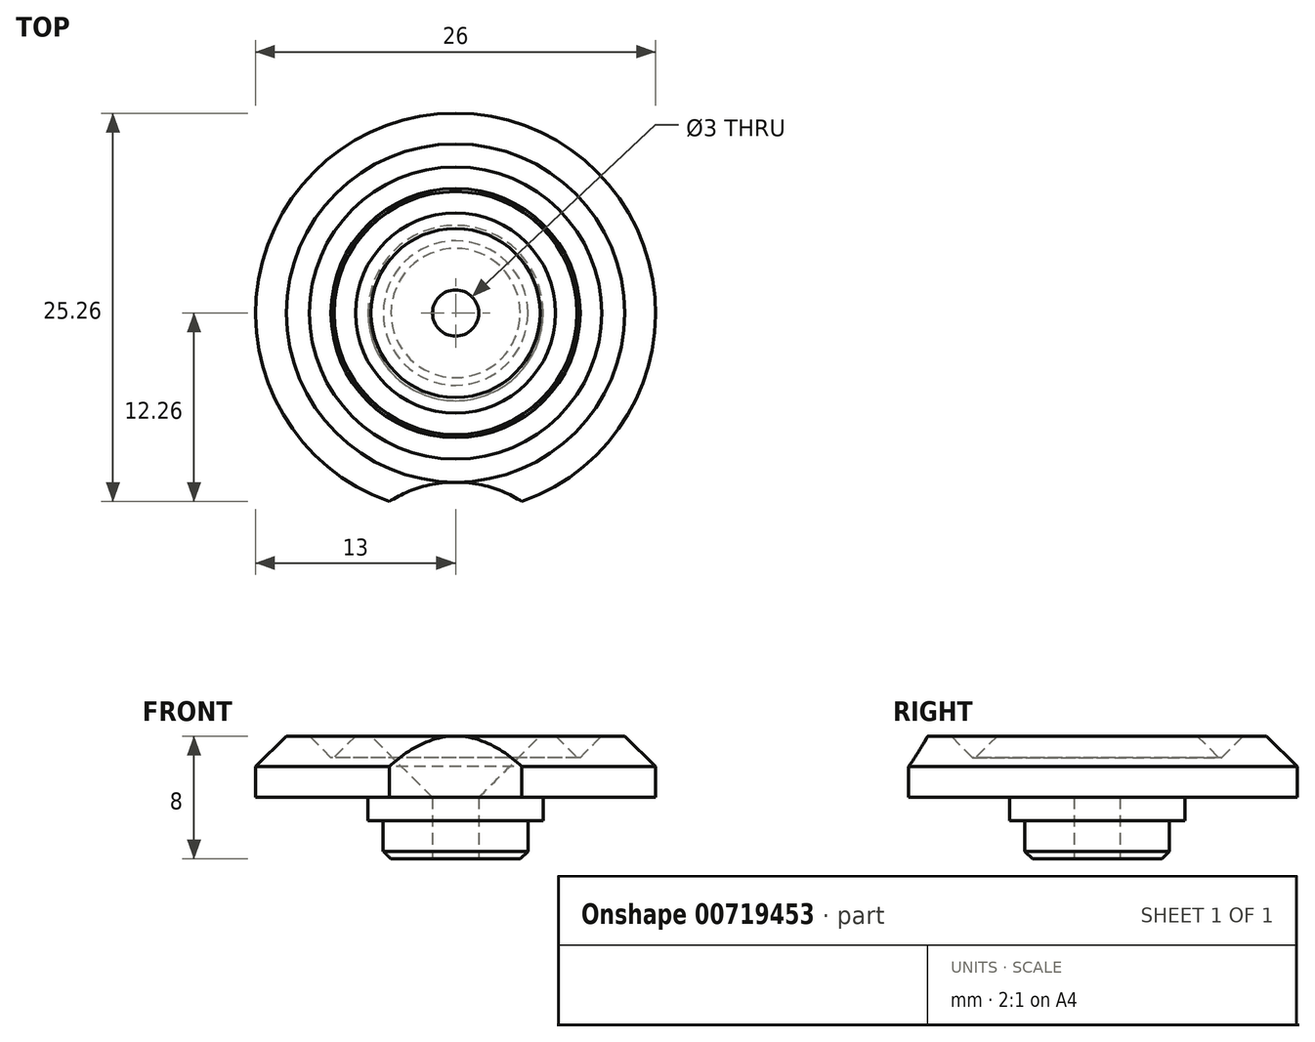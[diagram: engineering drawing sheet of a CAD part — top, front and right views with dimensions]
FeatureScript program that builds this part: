
annotation { "Feature Type Name" : "Feature", "Feature Type Description" : "" }
export const myFeature = defineFeature(function(context is Context, id is Id, definition is map)
    precondition{}
    {
        {
            var Q0;
            Q0=qCreatedBy(makeId("Top.planeOp"),FACE);
            var sketch = newSketch(context, id + "F0", { "sketchPlane" : qUnion([Q0])});
            skCircle(sketch, "E0", {"center": v(0, 0) * mm, "radius": 13 * mm});
            skLineSegment(sketch, "E1", {"start": v(0, 33.5) * mm, "end": v(0, -39.1) * mm, "construction": true});
            skLineSegment(sketch, "E2", {"start": v(30.36, 0) * mm, "end": v(-36.49, 0) * mm, "construction": true});
            skSolve(sketch);
        }
        {
            var Q0;
            Q0=qSketchRegion(id+"F0",true);
            extrude(context, id + "F1", {"entities" : qUnion([Q0]), "depth" : 4 * mm, "offsetDistance" : 25 * mm});
        }
        {
            var Q0;
            Q0=makeQuery(id+"F1.opExtrude","CAP_EDGE",EDGE,{"disambiguationData":[OSD([sQuery(id+"F0.wireOp",EDGE,"E0")])],"isStart":false});
            chamfer(context, id + "F2", {"entities" : qUnion([Q0]), "width" : 2 * mm, "tangentPropagation" : true});
        }
        {
            var Q0;
            Q0=makeQuery(id+"F1.opExtrude","CAP_FACE",FACE,{"disambiguationData":[OSD([sQuery(id+"F0.wireOp",EDGE,"E0")])],"isStart":true});
            var sketch = newSketch(context, id + "F3", { "sketchPlane" : qUnion([Q0])});
            skCircle(sketch, "E3", {"center": v(0, 0) * mm, "radius": 4.7 * mm});
            skSolve(sketch);
        }
        {
            var Q0;
            Q0=qSketchRegion(id+"F3",true);
            extrude(context, id + "F4", {"entities" : qUnion([Q0]), "operationType" : NewBodyOperationType.ADD, "depth" : 4 * mm, "offsetDistance" : 25 * mm});
        }
        {
            var Q0;
            Q0=makeQuery(id+"F4.opExtrude","CAP_EDGE",EDGE,{"disambiguationData":[OSD([sQuery(id+"F3.wireOp",EDGE,"E3")])],"isStart":false});
            chamfer(context, id + "F5", {"entities" : qUnion([Q0]), "width" : .5 * mm, "tangentPropagation" : true});
        }
        {
            var Q0;
            Q0=makeQuery(id+"F4.opExtrude","CAP_FACE",FACE,{"disambiguationData":[OSD([sQuery(id+"F3.wireOp",EDGE,"E3")])],"isStart":false});
            var sketch = newSketch(context, id + "F6", { "sketchPlane" : qUnion([Q0])});
            skCircle(sketch, "E4", {"center": v(0, 0) * mm, "radius": 1.5 * mm});
            skSolve(sketch);
        }
        {
            var Q0;
            Q0=qSketchRegion(id+"F6",true);
            extrude(context, id + "F7", {"entities" : qUnion([Q0]), "operationType" : NewBodyOperationType.REMOVE, "oppositeDirection" : true, "depth" : 25 * mm, "offsetDistance" : 25 * mm});
        }
        {
            var Q0;
            Q0=makeQuery(id+"F1.opExtrude","CAP_FACE",FACE,{"disambiguationData":[OSD([sQuery(id+"F0.wireOp",EDGE,"E0")])],"isStart":true});
            var sketch = newSketch(context, id + "F8", { "sketchPlane" : qUnion([Q0])});
            skCircle(sketch, "E5.0", {"center": v(0, 0) * mm, "radius": 5.7 * mm});
            skCircle(sketch, "E6.0", {"center": v(0, 0) * mm, "radius": 4.7 * mm});
            skSolve(sketch);
        }
        {
            var Q0;
            Q0=qSketchRegion(id+"F8",true);
            extrude(context, id + "F9", {"entities" : qUnion([Q0]), "operationType" : NewBodyOperationType.ADD, "depth" : 1.5 * mm, "offsetDistance" : 25 * mm});
        }
        {
            var Q0;
            Q0=makeQuery(id+"F1.opExtrude","CAP_FACE",FACE,{"disambiguationData":[OSD([sQuery(id+"F0.wireOp",EDGE,"E0")])],"isStart":true});
            var sketch = newSketch(context, id + "F10", { "sketchPlane" : qUnion([Q0])});
            skLineSegment(sketch, "E7", {"start": v(0, 15.67) * mm, "end": v(0, -20.26) * mm, "construction": true});
            skCircle(sketch, "E8.0", {"center": v(0, 0) * mm, "radius": 13 * mm, "construction": true});
            skCircle(sketch, "E9", {"center": v(0, 19) * mm, "radius": 8 * mm});
            skSolve(sketch);
        }
        {
            var Q0;
            Q0 = qSketchRegion(id + "F10", true);
            extrude(context, id + "F11", {"entities" : qUnion([Q0]), "operationType" : NewBodyOperationType.REMOVE, "oppositeDirection" : true, "depth" : 25 * mm, "offsetDistance" : 25 * mm});
        }
        {
            var Q0;
            Q0=makeQuery(id+"F1.opExtrude","CAP_FACE",FACE,{"disambiguationData":[OSD([sQuery(id+"F0.wireOp",EDGE,"E0")])],"isStart":false});
            var sketch = newSketch(context, id + "F12", { "sketchPlane" : qUnion([Q0])});
            skCircle(sketch, "E10", {"center": v(0, 0) * mm, "radius": 5 * mm});
            skCircle(sketch, "E11", {"center": v(0, 0) * mm, "radius": 6.5 * mm});
            skCircle(sketch, "E12", {"center": v(0, 0) * mm, "radius": 9.5 * mm});
            skSolve(sketch);
        }
        {
            var Q0;
            Q0=makeQuery(id+"F12.imprint","IMPRINT",FACE,{"disambiguationData":[TD([[makeQuery(id+"F12.imprint","IMPRINT",EDGE,{"derivedFrom":sQuery(id+"F12.wireOp",EDGE,"E11")}),-1.0]])]});
            extrude(context, id + "F13", {"entities" : qUnion([Q0]), "operationType" : NewBodyOperationType.REMOVE, "oppositeDirection" : true, "depth" : 1.4 * mm, "offsetDistance" : 25 * mm});
        }
        {
            var Q0;
            Q0=makeQuery(id+"F13.boolean.opBoolean","COPY",EDGE,{"derivedFrom":makeQuery(id+"F13.opExtrude","CAP_EDGE",EDGE,{"disambiguationData":[OSD([sQuery(id+"F12.wireOp",EDGE,"E12")])],"isStart":false})});
            var Q1;
            Q1=makeQuery(id+"F13.boolean.opBoolean","COPY",EDGE,{"derivedFrom":makeQuery(id+"F13.opExtrude","CAP_EDGE",EDGE,{"disambiguationData":[OSD([sQuery(id+"F12.wireOp",EDGE,"E11")])],"isStart":false})});
            chamfer(context, id + "F14", {"entities" : qUnion([Q0, Q1]), "width" : 1.4 * mm, "tangentPropagation" : true});
        }
        {
            var Q0;
            Q0=makeQuery(id+"F7.boolean.opBoolean","INTERSECT",EDGE,{"derivedFrom":[makeQuery(id+"F1.opExtrude","CAP_FACE",FACE,{"disambiguationData":[OSD([sQuery(id+"F0.wireOp",EDGE,"E0")])],"isStart":false}),makeQuery(id+"F7.opExtrude","SWEPT_FACE",FACE,{"disambiguationData":[OSD([sQuery(id+"F6.wireOp",EDGE,"E4")])]})]});
            chamfer(context, id + "F15", {"entities" : qUnion([Q0]), "width" : 4 * mm, "tangentPropagation" : true});
        }
    });
